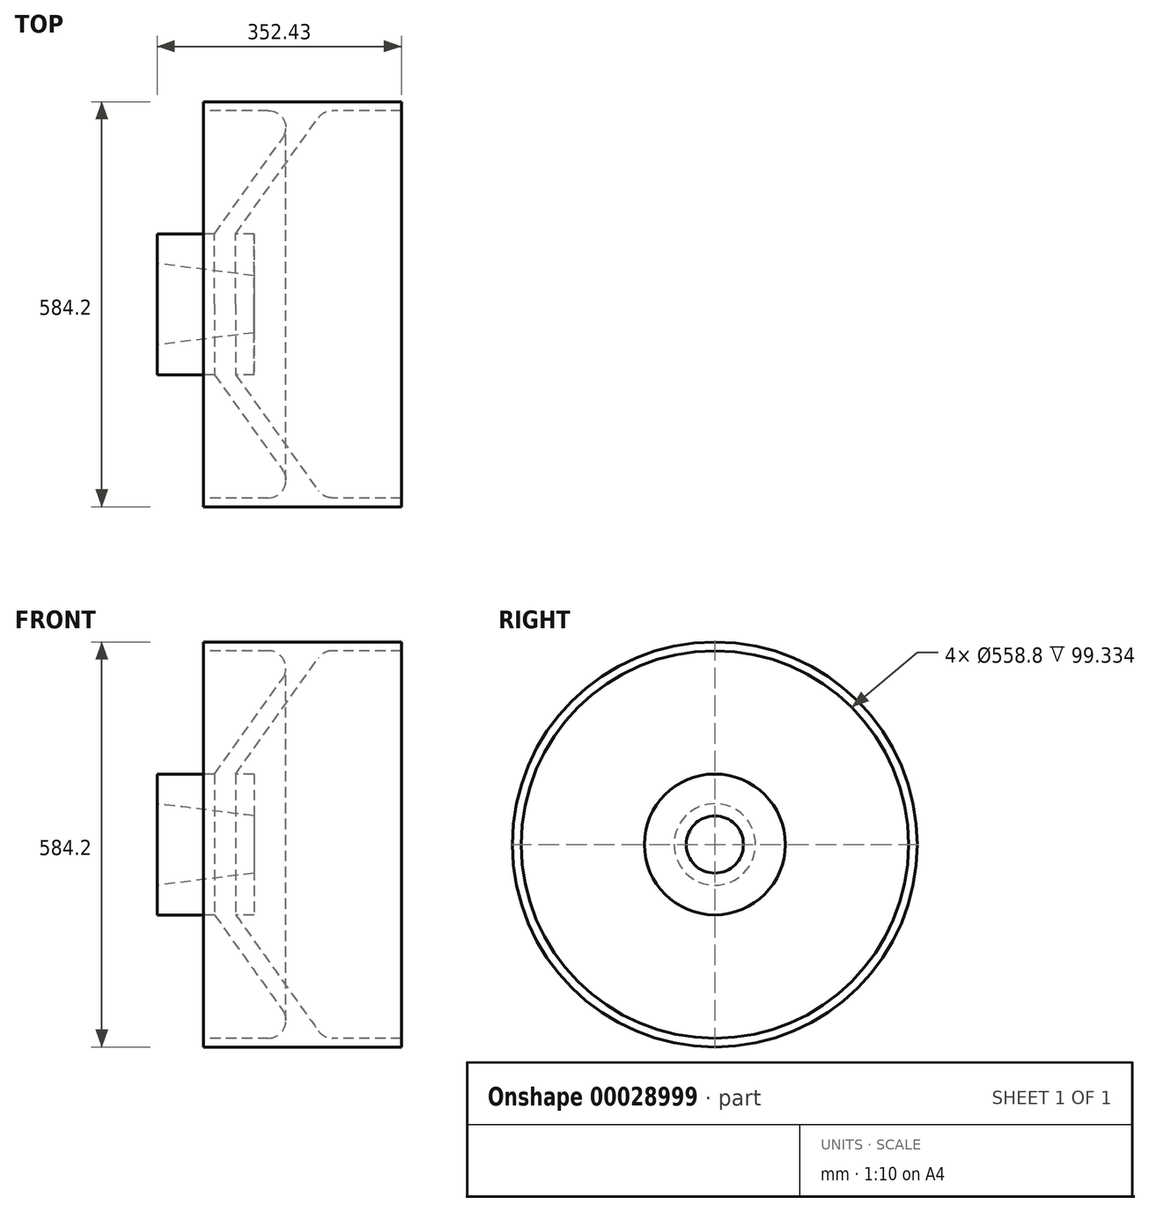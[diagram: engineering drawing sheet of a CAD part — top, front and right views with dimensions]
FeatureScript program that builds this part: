
annotation { "Feature Type Name" : "Feature", "Feature Type Description" : "" }
export const myFeature = defineFeature(function(context is Context, id is Id, definition is map)
    precondition{}
    {
        {
            var Q0;
            Q0=qCreatedBy(makeId("Front.planeOp"),FACE);
            var sketch = newSketch(context, id + "F0", { "sketchPlane" : qUnion([Q0])});
            skLineSegment(sketch, "E0", {"start": v(-118.82, 0) * mm, "end": v(123.9, 0) * mm, "construction": true});
            skLineSegment(sketch, "E1", {"start": v(0, 58.74) * mm, "end": v(0, -75.21) * mm, "construction": true});
            skLineSegment(sketch, "E2.bottom", {"start": v(-142.88, 292.1) * mm, "end": v(142.87, 292.1) * mm});
            skLineSegment(sketch, "E2.top", {"start": v(-142.88, 279.4) * mm, "end": v(142.87, 279.4) * mm});
            skLineSegment(sketch, "E2.left", {"start": v(-142.88, 292.1) * mm, "end": v(-142.88, 279.4) * mm});
            skLineSegment(sketch, "E2.right", {"start": v(142.87, 292.1) * mm, "end": v(142.87, 279.4) * mm});
            skLineSegment(sketch, "E3", {"start": v(0, 279.4) * mm, "end": v(0, 292.1) * mm, "construction": true});
            skLineSegment(sketch, "E4.bottom", {"start": v(-209.55, 101.6) * mm, "end": v(-69.85, 101.6) * mm});
            skLineSegment(sketch, "E4.top", {"start": v(-209.55, 58.74) * mm, "end": v(-69.85, 58.74) * mm});
            skLineSegment(sketch, "E4.left", {"start": v(-209.55, 101.6) * mm, "end": v(-209.55, 58.74) * mm});
            skLineSegment(sketch, "E4.right", {"start": v(-69.85, 101.6) * mm, "end": v(-69.85, 58.74) * mm});
            skLineSegment(sketch, "E5", {"start": v(-96.22, 101.6) * mm, "end": v(30.45, 279.4) * mm});
            skLineSegment(sketch, "E6", {"start": v(0, 279.4) * mm, "end": v(-126.67, 101.6) * mm});
            skLineSegment(sketch, "E7", {"start": v(-69.85, 58.74) * mm, "end": v(-69.85, 41.28) * mm});
            skLineSegment(sketch, "E8", {"start": v(-69.85, 41.27) * mm, "end": v(-209.55, 58.74) * mm});
            skSolve(sketch);
        }
        {
            var Q0;
            Q0 = qSketchRegion(id + "F0", true);
            var Q1;
            Q1=sQuery(id+"F0.wireOp",EDGE,"E0");
            revolve(context, id + "F1", {"entities" : qUnion([Q0]), "axis" : qUnion([Q1]), "revolveType" : RevolveType.FULL});
        }
        {
            var Q0;
            Q0=makeQuery(id+"F1.opRevolve","SWEPT_EDGE",EDGE,{"disambiguationData":[OSD([sQuery(id+"F0.wireOp",EDGE,"E2.top"),sQuery(id+"F0.wireOp",EDGE,"E5")])]});
            var Q1;
            Q1=makeQuery(id+"F1.opRevolve","SWEPT_EDGE",EDGE,{"disambiguationData":[OSD([sQuery(id+"F0.wireOp",EDGE,"E2.top"),sQuery(id+"F0.wireOp",EDGE,"E6")])]});
            fillet(context, id + "F2", {"entities" : qUnion([Q0, Q1]), "radius" : 25.4 * mm, "tangentPropagation" : true, "allowEdgeOverflow" : false});
        }
    });
